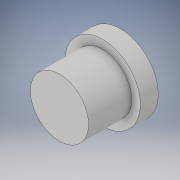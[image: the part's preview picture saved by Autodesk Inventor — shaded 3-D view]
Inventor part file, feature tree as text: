
AUTODESK INVENTOR PART (.ipt)
format: ipt  version: 2019 (Build 230136000, 136)  size: 103,936 bytes
history: native  units: in
note: dims shown in document units (in); Inventor stores cm internally (conversion verified against a paired STEP export)
features: extrude x2, sketch x2
ambient origin geometry x8: Origin, YZ Plane, XZ Plane, XY Plane, X Axis, Y Axis, Z Axis, Center Point
bodies: Solid1 (feature_tree)
feature tree (4):
  extrude  "Extrusion1"  Depth=0.125in TaperAngle=0.0deg
  extrude  "Extrusion2"  Depth=0.3in TaperAngle=0.0deg
  sketch  "Sketch1"  dims[d0=0.525in d1=0.125in d2=0.0in]
  sketch  "Sketch2"  dims[d3=0.405in d4=0.3in d5=0.0in]
